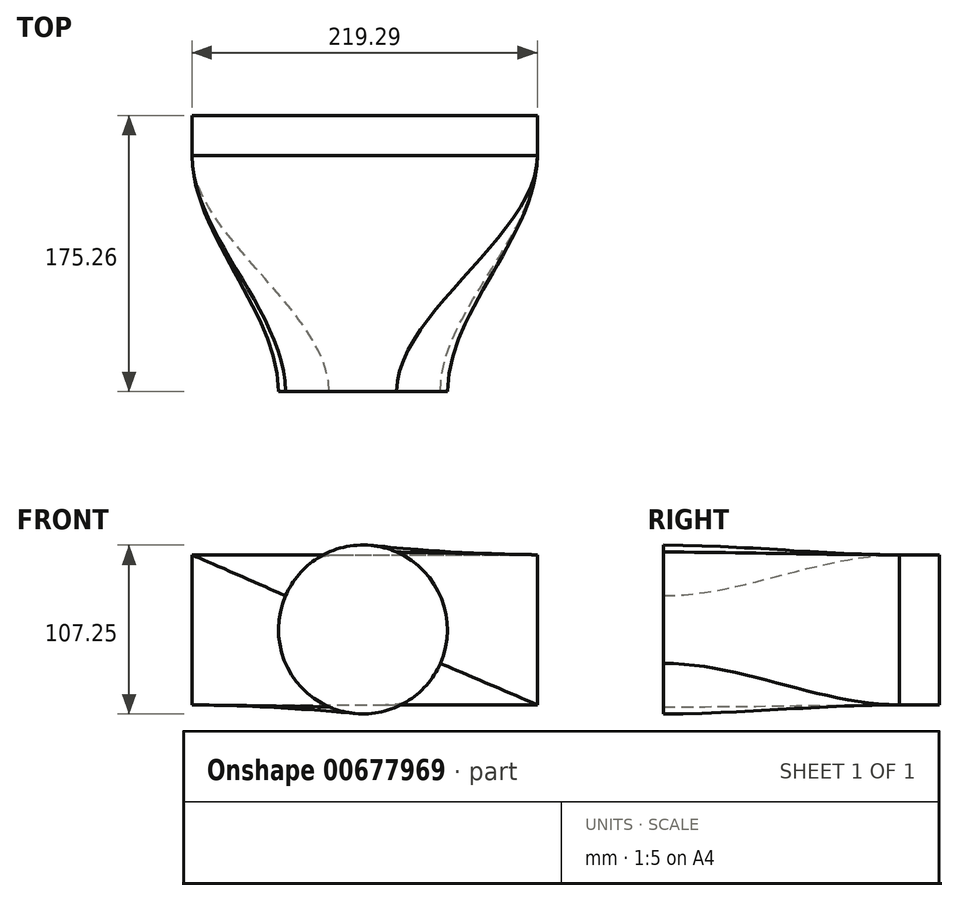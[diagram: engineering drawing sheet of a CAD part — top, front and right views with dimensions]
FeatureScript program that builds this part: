
annotation { "Feature Type Name" : "Feature", "Feature Type Description" : "" }
export const myFeature = defineFeature(function(context is Context, id is Id, definition is map)
    precondition{}
    {
        {
            var Q0;
            Q0=qCreatedBy(makeId("Front.planeOp"),FACE);
            var sketch = newSketch(context, id + "F0", { "sketchPlane" : qUnion([Q0])});
            skLineSegment(sketch, "E0.bottom", {"start": v(-113.93, 37.84) * mm, "end": v(105.36, 37.84) * mm});
            skLineSegment(sketch, "E0.top", {"start": v(-113.93, -57.47) * mm, "end": v(105.36, -57.47) * mm});
            skLineSegment(sketch, "E0.left", {"start": v(-113.93, 37.84) * mm, "end": v(-113.93, -57.47) * mm});
            skLineSegment(sketch, "E0.right", {"start": v(105.36, 37.84) * mm, "end": v(105.36, -57.47) * mm});
            skSolve(sketch);
        }
        {
            var Q0;
            Q0 = qSketchRegion(id + "F0", true);
            extrude(context, id + "F1", {"entities" : qUnion([Q0]), "depth" : 25.4 * mm, "offsetDistance" : 25.4 * mm});
        }
        {
            var Q0;
            Q0=qCreatedBy(makeId("Front.planeOp"),FACE);
            cPlane(context, id + "F2", {"entities" : qUnion([Q0]), "cplaneType" : CPlaneType.OFFSET, "offset" : 175.26 * mm, "width" : 152.4 * mm, "height" : 152.4 * mm});
        }
        {
            var Q0;
            Q0=qCreatedBy(id+"F2.planeOp",FACE);
            var sketch = newSketch(context, id + "F3", { "sketchPlane" : qUnion([Q0])});
            skCircle(sketch, "E1", {"center": v(-5.47, -9.58) * mm, "radius": 53.62 * mm});
            skSolve(sketch);
        }
        {
            var Q0;
            Q0=makeQuery(id+"F3.imprint","IMPRINT",FACE,{"disambiguationData":[TD([[makeQuery(id+"F3.imprint","IMPRINT",EDGE,{"derivedFrom":sQuery(id+"F3.wireOp",EDGE,"E1")}),1.0]])]});
            var Q1;
            Q1=makeQuery(id+"F1.opExtrude","CAP_FACE",FACE,{"disambiguationData":[OSD([sQuery(id+"F0.wireOp",EDGE,"E0.bottom"),sQuery(id+"F0.wireOp",EDGE,"E0.top"),sQuery(id+"F0.wireOp",EDGE,"E0.left"),sQuery(id+"F0.wireOp",EDGE,"E0.right")])],"isStart":false});
            loft(context, id + "F4", {"startCondition" : LoftEndDerivativeType.NORMAL_TO_PROFILE, "startMagnitude" : 1, "endCondition" : LoftEndDerivativeType.NORMAL_TO_PROFILE, "endMagnitude" : 1, "sheetProfilesArray" : [{ "sheetProfileEntities" : qUnion([Q0]) }, { "sheetProfileEntities" : qUnion([Q1]) }]});
        }
    });
